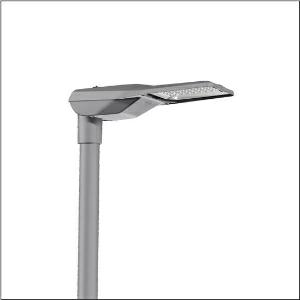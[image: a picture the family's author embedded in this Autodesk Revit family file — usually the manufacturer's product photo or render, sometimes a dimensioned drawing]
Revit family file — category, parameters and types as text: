
# Revit family: streetlight_sl_21_iq_mini___st1_0ab_5xe2m31v08gb_27e0
name_source: partatom
category: Lighting Fixtures
units: mm (PartAtom-declared; Revit-internal decimal feet)

## family parameters
Cut with Voids When Loaded = No
Host = Face
Light Source = No
Part Type = Normal
Room Calculation Point = No
Round Connector Dimension = Use Diameter
Shared = No

## types (1)
- --- (1 x LED, 5270 lm, 39.8 W, 3000K)
    Apparent Load = 40 VA
    CIE Flux Codes = 38 73 97 100 100
    Color Rendering = 70
    Color Temperature = 3000K
    Default Elevation = 1800 mm
    Description = Streetlight SL 21 iQ mini, mast luminaire, primary light control with lens, of PMMA, primary optical cover: cover, of toughened safety glass, transparent, light distribution: ST1.0aB, light emission: direct distribution, primary light characteristic: asymmetric, installation type: post-top, side-entry, LED, High Power LED, rated luminous flux: 5.270lm, luminous efficacy: 132lm/W, light colour: 730, colour temperature: 3000K, control gear: iQ-Street Remote, D4i with power reduction, control: pre-setting: logarithmic dimming characteristic, Street-Remote, Auto-Match, Temp-Guard, Lumen-Switch, Night-Set, Smart-Wire, Light-Fading, Desk-Remote (wireless, voltage-free reading and setting of iQ features in the workshop via application-optimized NFC function/RFID function), optimised constant luminous flux control (CLO 2.0), mains connection: 220..240V, AC, 50/60Hz, start of lifetime: 40W, end of service life: 41W, reduction: 18W, luminaire housing, of diecast aluminium, powder-coated, SITECO metallic grey (DB 702S), corrosivity category C5 high according to DIN EN ISO 12944, please order mast flange separately, inclination adjustable: 0°, 5°, 10°, 15°, sealing non-destructively replaceable, multi-level sealing system, length: 628mm, width: 235mm, height: 110mm, mast flange for spigot size: 42mm (side-entry): 5XC10008XM4, 60/48mm (side-entry/post-top): 5XC10108XM2, 76/60mm (side-entry/post-top): 5XC10108XM1, mounting height: 4..8m, Smart Interface above, protection rating (complete): IP66, insulation class (complete): insulation class II (safety insulation), certification: CE, ENEC, ENEC+, VDE, impact resistance: IK10, permissible operating ambient temperature for outdoor applications: -40..+50°C, standard-compliant lighting for roads and squares, packaging unit: 1 piece

Light Distribution: ST1.0aB
    Height = 110 mm
    Lamp = 1 x LED
    Lamp Light Flux = 5270 lm
    Lamp Power = 39.8 W
    Lamp count = 1
    Length = 625 mm
    Luminous efficacy = 132 lm/W
    Manufacturer = Siteco
    ModVariant = No
    Model = 5XE2M31V08GB
    Mounting Place = Pole
    Mounting Type = Pole top
    Number of Poles = 1
    OnlyDefault = Yes
    Power Factor = 1
    Product Name = Streetlight SL 21 iQ mini | ST1.0aB
    Product group = mast luminaire | pylon top
    ProductGroupID = 6100
    Protection Class = Protection class II
    Protection Degree = IP 66
    RLX_Detail_Level = 1
    RLX_Emergency_Light_Flux = 0 lm
    RLX_Emergency_Type = 0
    RLX_Emergency_Type_DB = No
    RlxData = <blob elided: 92665 chars, md5=74e0320c>
    Socket = socket
    Standby Power = 0 W
    System Light Flux = 5270 lm
    System Power = 40 W
    Type Comments = factory setting: luminous flux: 100 % | dim-lin: 254 | 800 mA
    Type Image = l_1003515.jpg
    URL = http://relux.com
    VarID = @adj_114063
    Voltage = 0 V
    Weight = 0.00 kg
    Width = 234 mm

## geometry (parser evidence)
native form markers: Blend x4, Sweep x11
no freeform markers — native parametric forms only
